# Revit family: QF_Summit_ARS32PVBIADA_Pharma_Vac_ADA_Compliant_Commercial_All_Refrigerator
name_source: partatom
category: Specialty Equipment
units: mm (PartAtom-declared; Revit-internal decimal feet)

## family parameters
Always vertical = Yes
Cut with Voids When Loaded = No
Part Type = Normal
Room Calculation Point = No
Round Connector Dimension = Use Diameter
Shared = No
Work Plane-Based = No

## types (1)
- QF_Summit_ARS32PVBIADA_Pharma_Vac_ADA_Compliant_Commercial_All_Refrigerator
    Apparent Power = 86 VA
    BTUH = 0.0 Btu/h
    Conn Conduit = Yes
    Cycle = 60 Hz
    Default Elevation = 0"
    Depth = 22 5/8"
    Description = Pharma-Vac ADA Compliant Commercial All-Refrigerator
    Elec Conn Connection Height = 0"
    Elec Conn RI Height = 0"
    FL Amps = 1 A
    Foodservice Equipment Identifier = Yes
    Height = 32"
    Identify Quantity as Lot = Yes
    Length = 19 3/4"
    Manufacturer = Summit
    Max Overcurrent Protection = 0 A
    Min Ckt Ampacity = 0 A
    Model = ARS32PVBIADA
    Number of Poles = 1
    Phase = 1
    Refrigerant Type = R600a
    Refrigerant Volume = 0.00 kip
    Volts = 115 V
    Watts = 86 W
    Weight in Pounds = 102

## geometry (parser evidence)
native form markers: Sweep x3
no freeform markers — native parametric forms only
